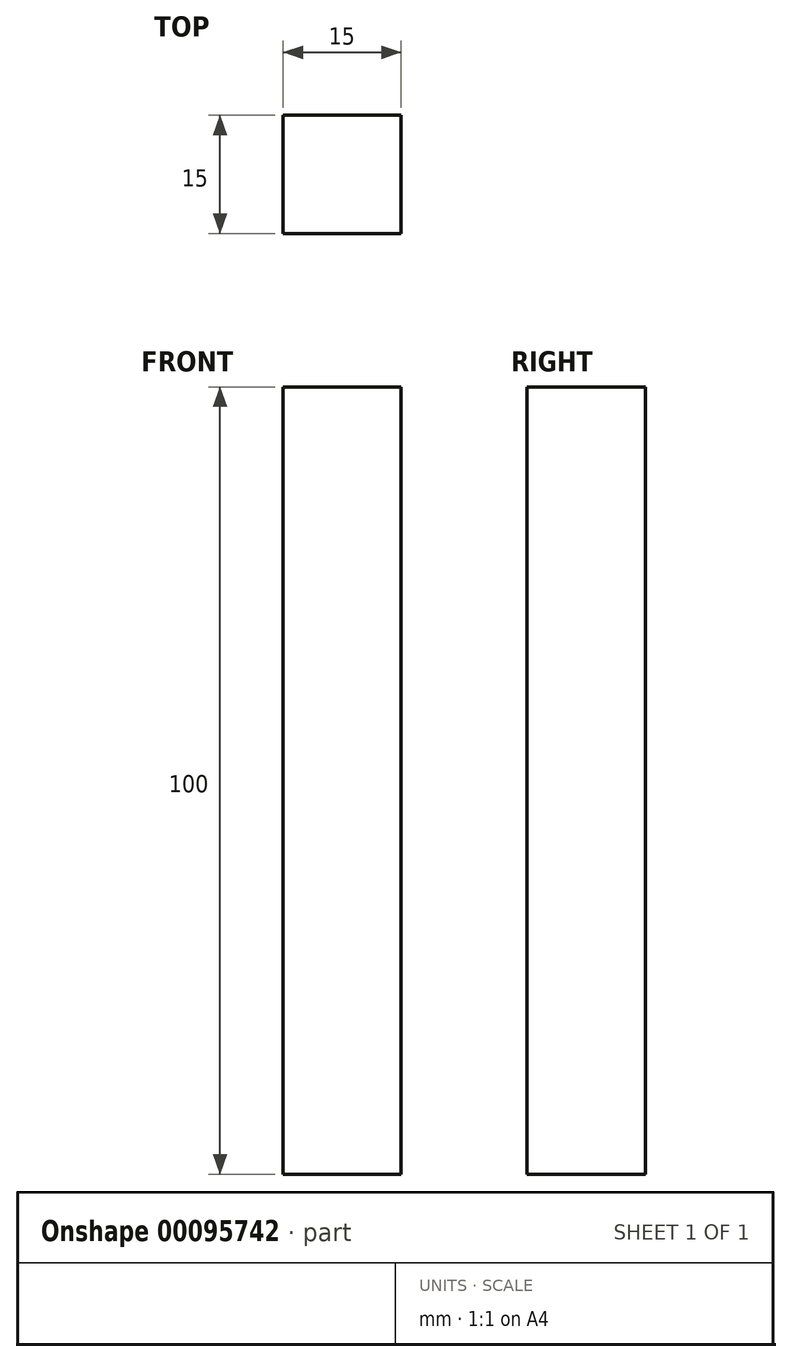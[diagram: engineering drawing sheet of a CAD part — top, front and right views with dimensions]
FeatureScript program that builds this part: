
annotation { "Feature Type Name" : "Feature", "Feature Type Description" : "" }
export const myFeature = defineFeature(function(context is Context, id is Id, definition is map)
    precondition{}
    {
        {
            var Q0;
            Q0=qCreatedBy(makeId("Front.planeOp"),FACE);
            var sketch = newSketch(context, id + "F0", { "sketchPlane" : qUnion([Q0])});
            skLineSegment(sketch, "E0.bottom", {"start": v(7.5, -50) * mm, "end": v(-7.5, -50) * mm});
            skLineSegment(sketch, "E0.top", {"start": v(7.5, 50) * mm, "end": v(-7.5, 50) * mm});
            skLineSegment(sketch, "E0.left", {"start": v(7.5, -50) * mm, "end": v(7.5, 50) * mm});
            skLineSegment(sketch, "E0.right", {"start": v(-7.5, -50) * mm, "end": v(-7.5, 50) * mm});
            skPoint(sketch, "E0.middle", {"position": v(0, 0) * mm});
            skSolve(sketch);
        }
        {
            var Q0;
            Q0 = qSketchRegion(id + "F0", true);
            extrude(context, id + "F1", {"entities" : qUnion([Q0]), "endBound" : BoundingType.SYMMETRIC, "depth" : 15 * mm});
        }
    });
